# Revit family: PRE030049
name_source: partatom
category: Appareils sanitaires
revit_build: Autodesk Revit 2015 (Build: 20140606_1530(x64)
units: mm (PartAtom-declared; Revit-internal decimal feet)

## types (6) — shared parameters
Bleu = PRESTO Bleu
Chrome = PRESTO Chrome
Diamètre nominal = 20 mm  [stored 0.0656168 ft]
Elévation par défaut = 1219 mm
Perte de charge = 100.0 Pa
Rouge = PRESTO Rouge

## per-type parameters (varying)
| type | Equerres | Polantis code | Poussoir inox | Poussoir noir |
| 35814 Presto ALPA - ALPA S Seul mitigeur | Oui | PRE030049 | Oui | Non |
| 35013 Presto ALPA  - ALPA S Seul mitigeur | Oui | PRE030049a | Non | Oui |
| 35925 Presto ALPA  - ALPA S Seul mitigeur | Non | PRE030049b | Oui | Non |
| 35011 Presto ALPA  - ALPA S Seul mitigeur | Non | PRE030049c | Non | Oui |
| 35168 Presto ALPA  - ALPA S Seul mitigeur | Oui | PRE030049d | Oui | Non |
| 35166 Presto ALPA  - ALPA S Seul mitigeur | Non | PRE030049e | Oui | Non |

note: [stored X ft] marks values corroborated as IEEE doubles in the binary element streams (Revit-internal decimal feet)

## geometry (parser evidence)
native form markers: Blend x34, Sweep x30
no freeform markers — native parametric forms only
